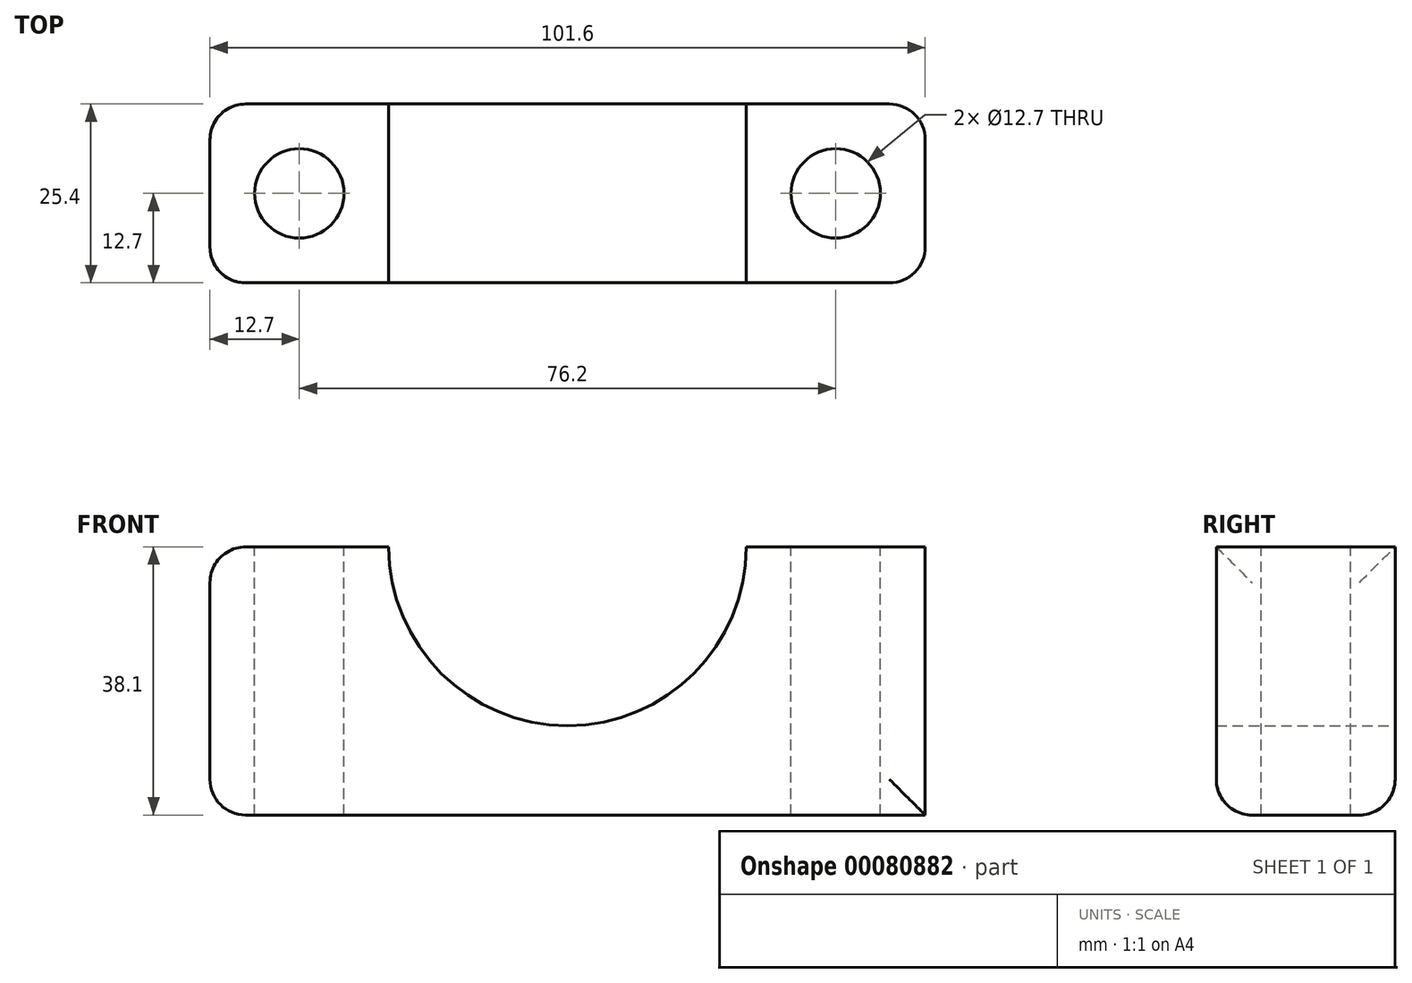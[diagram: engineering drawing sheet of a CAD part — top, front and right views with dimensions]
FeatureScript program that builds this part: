
annotation { "Feature Type Name" : "Feature", "Feature Type Description" : "" }
export const myFeature = defineFeature(function(context is Context, id is Id, definition is map)
    precondition{}
    {
        {
            var Q0;
            Q0=qCreatedBy(makeId("Front.planeOp"),FACE);
            var sketch = newSketch(context, id + "F0", { "sketchPlane" : qUnion([Q0])});
            skLineSegment(sketch, "E0.bottom", {"start": v(-50.8, 19.05) * mm, "end": v(-25.4, 19.05) * mm});
            skLineSegment(sketch, "E0.top", {"start": v(-50.8, -19.05) * mm, "end": v(50.8, -19.05) * mm});
            skLineSegment(sketch, "E0.left", {"start": v(-50.8, 19.05) * mm, "end": v(-50.8, -19.05) * mm});
            skLineSegment(sketch, "E0.right", {"start": v(50.8, 19.05) * mm, "end": v(50.8, -19.05) * mm});
            skPoint(sketch, "E0.middle", {"position": v(0, 0) * mm});
            skArc(sketch, "E1", {"start": v(-25.4, 19.05) * mm, "mid": v(0, -6.35) * mm, "end": v(25.4, 19.05) * mm});
            skLineSegment(sketch, "E2.trimOffspring", {"start": v(25.4, 19.05) * mm, "end": v(50.8, 19.05) * mm});
            skSolve(sketch);
        }
        {
            var Q0;
            Q0=makeQuery(id+"F0.imprint","IMPRINT",FACE,{"disambiguationData":[TD([[makeQuery(id+"F0.imprint","IMPRINT",EDGE,{"derivedFrom":sQuery(id+"F0.wireOp",EDGE,"E0.bottom")}),-1.0]])]});
            extrude(context, id + "F1", {"entities" : qUnion([Q0]), "depth" : 25.4 * mm});
        }
        {
            var Q0;
            Q0=makeQuery(id+"F1.opExtrude","SWEPT_FACE",FACE,{"disambiguationData":[OSD([sQuery(id+"F0.wireOp",EDGE,"E0.bottom")])]});
            var sketch = newSketch(context, id + "F2", { "sketchPlane" : qUnion([Q0])});
            skCircle(sketch, "E3", {"center": v(-38.1, -12.7) * mm, "radius": 6.35 * mm});
            skCircle(sketch, "E4.MirrorC", {"center": v(38.1, -12.7) * mm, "radius": 6.35 * mm});
            skSolve(sketch);
        }
        {
            var Q0;
            Q0=sQuery(id+"F2.wireOp",VERTEX,"E3.center");
            var Q1;
            Q1=makeQuery(id+"F1.opExtrude","SWEPT_BODY",BODY,{"disambiguationData":[OSD([sQuery(id+"F0.wireOp",EDGE,"E0.bottom"),sQuery(id+"F0.wireOp",EDGE,"E0.top"),sQuery(id+"F0.wireOp",EDGE,"E0.left"),sQuery(id+"F0.wireOp",EDGE,"E0.right"),sQuery(id+"F0.wireOp",EDGE,"E1"),sQuery(id+"F0.wireOp",EDGE,"E2.trimOffspring")])]});
            hole(context, id + "F3", {"style" : HoleStyle.SIMPLE, "endStyle" : HoleEndStyle.THROUGH, "holeDiameter" : 12.7 * mm, "locations" : qUnion([Q0]), "scope" : qUnion([Q1]), "isTappedThrough" : true});
        }
        {
            var Q0;
            Q0=sQuery(id+"F2.wireOp",VERTEX,"E4.MirrorC.center");
            var Q1;
            Q1=makeQuery(id+"F1.opExtrude","SWEPT_BODY",BODY,{"disambiguationData":[OSD([sQuery(id+"F0.wireOp",EDGE,"E0.bottom"),sQuery(id+"F0.wireOp",EDGE,"E0.top"),sQuery(id+"F0.wireOp",EDGE,"E0.left"),sQuery(id+"F0.wireOp",EDGE,"E0.right"),sQuery(id+"F0.wireOp",EDGE,"E1"),sQuery(id+"F0.wireOp",EDGE,"E2.trimOffspring")])]});
            hole(context, id + "F4", {"style" : HoleStyle.SIMPLE, "endStyle" : HoleEndStyle.THROUGH, "holeDiameter" : 12.7 * mm, "locations" : qUnion([Q0]), "scope" : qUnion([Q1]), "isTappedThrough" : true});
        }
        {
            var Q0;
            Q0=makeQuery(id+"F1.opExtrude","CAP_EDGE",EDGE,{"disambiguationData":[OSD([sQuery(id+"F0.wireOp",EDGE,"E0.right")])],"isStart":true});
            var Q1;
            Q1=makeQuery(id+"F1.opExtrude","CAP_EDGE",EDGE,{"disambiguationData":[OSD([sQuery(id+"F0.wireOp",EDGE,"E0.left")])],"isStart":true});
            var Q2;
            Q2=makeQuery(id+"F1.opExtrude","CAP_EDGE",EDGE,{"disambiguationData":[OSD([sQuery(id+"F0.wireOp",EDGE,"E0.top")])],"isStart":true});
            var Q3;
            Q3=makeQuery(id+"F1.opExtrude","SWEPT_EDGE",EDGE,{"disambiguationData":[OSD([sQuery(id+"F0.wireOp",EDGE,"E0.top"),sQuery(id+"F0.wireOp",EDGE,"E0.left")])]});
            var Q4;
            Q4=makeQuery(id+"F1.opExtrude","SWEPT_FACE",FACE,{"disambiguationData":[OSD([sQuery(id+"F0.wireOp",EDGE,"E0.left")])]});
            var Q5;
            Q5=makeQuery(id+"F1.opExtrude","CAP_EDGE",EDGE,{"disambiguationData":[OSD([sQuery(id+"F0.wireOp",EDGE,"E0.top")])],"isStart":false});
            var Q6;
            Q6=makeQuery(id+"F1.opExtrude","CAP_EDGE",EDGE,{"disambiguationData":[OSD([sQuery(id+"F0.wireOp",EDGE,"E0.right")])],"isStart":false});
            fillet(context, id + "F5", {"entities" : qUnion([Q0, Q1, Q2, Q3, Q4, Q5, Q6]), "radius" : 5.08 * mm, "tangentPropagation" : true, "allowEdgeOverflow" : false});
        }
    });
